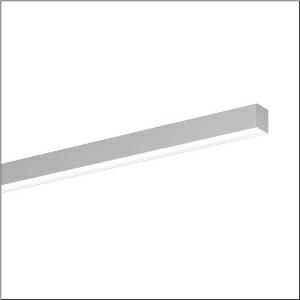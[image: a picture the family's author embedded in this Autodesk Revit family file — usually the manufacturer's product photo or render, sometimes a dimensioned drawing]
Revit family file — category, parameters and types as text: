
# Revit family: silica_r__21_51mx20tct5s_f80a
name_source: partatom
category: Lighting Fixtures
units: mm (PartAtom-declared; Revit-internal decimal feet)

## family parameters
Cut with Voids When Loaded = No
Host = Face
Light Source = No
Part Type = Normal
Room Calculation Point = No
Round Connector Dimension = Use Diameter
Shared = No

## types (1)
- --- (1 x LED, 6000 lm, 51.3 W, 6500K)
    Apparent Load = 51 VA
    CIE Flux Codes = 48 79 96 100 100
    Color Rendering = 80
    Color Temperature = 6500K
    Default Elevation = 1800 mm
    Description = Silica® 21, office luminaire, primary optical cover: cover, of PMMA, opal, light emission: direct distribution, primary light characteristic: symmetric, installation type: surface-mounted, LED, rated luminous flux: 6.000lm, luminous efficacy: 112lm/W, light colour: 8tw, colour temperature: 2700..6500K, control gear: DALI DT8, with terminal, 3+2-pole, max. 2.5mm², mains connection: 220..240V, AC, 50/60Hz, rated input power: 53.8W, luminaire housing, of aluminium, metallic grey (RAL 9006), length: 3.004mm, width: 53mm, height: 53mm, protection rating (complete): IP20, insulation class (complete): insulation class I (protective earthing), certification: CE, permissible operating ambient temperature: 0..+35°C, standard: EN 50419, packaging unit: 1 piece
    Height = 53 mm
    Lamp = 1 x LED
    Lamp Light Flux = 6000 lm
    Lamp Power = 51.3 W
    Lamp count = 1
    Length = 3004 mm
    Luminous efficacy = 117 lm/W
    Manufacturer = Siteco
    ModVariant = No
    Model = 51MX20TCT5S
    Mounting Place = Ceiling
    Mounting Type = Surface mounted
    Number of Poles = 1
    OnlyDefault = Yes
    Power Factor = 1
    Product Name = Silica® 21
    Product group = office luminaire | ceiling mounted
    ProductGroupID = 302
    Protection Class = Protection class I
    Protection Degree = IP 20
    RLX_Detail_Level = 1
    RLX_Emergency_Light_Flux = 0 lm
    RLX_Emergency_Type = 0
    RLX_Emergency_Type_DB = No
    RlxData = <blob elided: 23153 chars, md5=373fa36d>
    Socket = socket
    Standby Power = 0 W
    System Light Flux = 6000 lm
    System Power = 51 W
    Type Comments = individual setting
    Type Image = l_1335933.jpg
    URL = http://relux.com
    VarID = @adj_139662
    Voltage = 0 V
    Weight = 0.00 kg
    Width = 53 mm

## geometry (parser evidence)
native form markers: Blend x4, Sweep x10
no freeform markers — native parametric forms only
